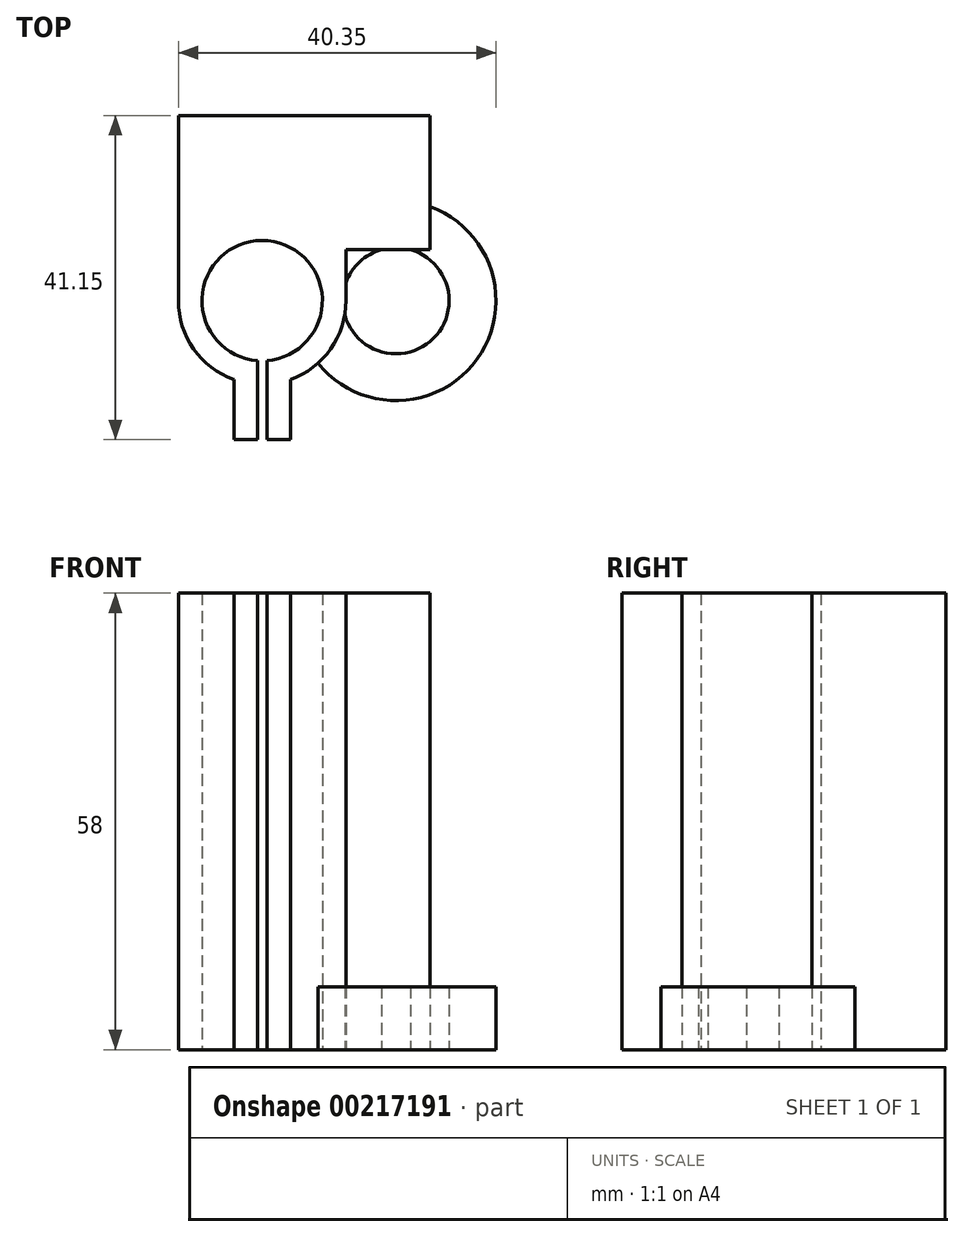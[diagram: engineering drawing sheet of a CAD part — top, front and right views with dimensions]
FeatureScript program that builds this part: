
annotation { "Feature Type Name" : "Feature", "Feature Type Description" : "" }
export const myFeature = defineFeature(function(context is Context, id is Id, definition is map)
    precondition{}
    {
        {
            var Q0;
            Q0=qCreatedBy(makeId("Top.planeOp"),FACE);
            var sketch = newSketch(context, id + "F0", { "sketchPlane" : qUnion([Q0])});
            skCircle(sketch, "E0", {"center": v(0, 0) * mm, "radius": 7.65 * mm});
            skCircle(sketch, "E1.0", {"center": v(0, 0) * mm, "radius": 10.65 * mm});
            skLineSegment(sketch, "E2", {"start": v(-0.6, -7.63) * mm, "end": v(-0.6, -17.65) * mm});
            skLineSegment(sketch, "E3", {"start": v(-0.6, -17.65) * mm, "end": v(-3.6, -17.65) * mm});
            skLineSegment(sketch, "E4", {"start": v(-3.6, -17.65) * mm, "end": v(-3.6, -10.03) * mm});
            skLineSegment(sketch, "E5.MirrorCS", {"start": v(0.6, -7.63) * mm, "end": v(0.6, -17.65) * mm});
            skLineSegment(sketch, "E6.MirrorCS", {"start": v(0.6, -17.65) * mm, "end": v(3.6, -17.65) * mm});
            skLineSegment(sketch, "E7.MirrorCS", {"start": v(3.6, -17.65) * mm, "end": v(3.6, -10.03) * mm});
            skLineSegment(sketch, "E8", {"start": v(21.35, 6.5) * mm, "end": v(21.35, 23.5) * mm});
            skLineSegment(sketch, "E9", {"start": v(-10.65, 0) * mm, "end": v(-10.65, 23.5) * mm});
            skLineSegment(sketch, "E10", {"start": v(-10.65, 23.5) * mm, "end": v(21.35, 23.5) * mm});
            skLineSegment(sketch, "E11", {"start": v(21.35, 6.5) * mm, "end": v(10.65, 6.5) * mm});
            skLineSegment(sketch, "E12", {"start": v(10.65, 0) * mm, "end": v(10.65, 6.5) * mm});
            skSolve(sketch);
        }
        {
            var Q0;
            Q0=makeQuery(id+"F0.imprint","IMPRINT",FACE,{"disambiguationData":[TD([[makeQuery(id+"F0.imprint","IMPRINT",EDGE,{"derivedFrom":sQuery(id+"F0.wireOp",EDGE,"E8")}),1.0]])]});
            var Q1;
            {var subQ2=sQuery(id+"F0.wireOp",EDGE,"E2");var subQ6=sQuery(id+"F0.wireOp",EDGE,"E0");var subQ7=makeQuery(id+"F0.imprint","INTERSECT",VERTEX,{"derivedFrom":[subQ6,subQ2]});Q1=makeQuery(id+"F0.imprint","IMPRINT",FACE,{"disambiguationData":[TD([[makeQuery(id+"F0.imprint","IMPRINT",EDGE,{"disambiguationData":[TD([[subQ7,1.0]])],"derivedFrom":subQ6}),-1.0]])]});}
            var Q2;
            {var subQ4=sQuery(id+"F0.wireOp",EDGE,"E6.MirrorCS");Q2=makeQuery(id+"F0.imprint","IMPRINT",FACE,{"disambiguationData":[TD([[makeQuery(id+"F0.imprint","IMPRINT",EDGE,{"derivedFrom":subQ4}),1.0]])]});}
            var Q3;
            {var subQ4=sQuery(id+"F0.wireOp",EDGE,"E3");Q3=makeQuery(id+"F0.imprint","IMPRINT",FACE,{"disambiguationData":[TD([[makeQuery(id+"F0.imprint","IMPRINT",EDGE,{"derivedFrom":subQ4}),-1.0]])]});}
            extrude(context, id + "F1", {"entities" : qUnion([Q0, Q1, Q2, Q3]), "depth" : 58 * mm});
        }
        {
            var Q0;
            Q0=makeQuery(id+"F1.opExtrude","CAP_FACE",FACE,{"disambiguationData":[OSD([sQuery(id+"F0.wireOp",EDGE,"E0"),sQuery(id+"F0.wireOp",EDGE,"E1.0"),sQuery(id+"F0.wireOp",EDGE,"E2"),sQuery(id+"F0.wireOp",EDGE,"E3"),sQuery(id+"F0.wireOp",EDGE,"E4"),sQuery(id+"F0.wireOp",EDGE,"E5.MirrorCS"),sQuery(id+"F0.wireOp",EDGE,"E6.MirrorCS"),sQuery(id+"F0.wireOp",EDGE,"E7.MirrorCS"),sQuery(id+"F0.wireOp",EDGE,"E8"),sQuery(id+"F0.wireOp",EDGE,"E9"),sQuery(id+"F0.wireOp",EDGE,"E10"),sQuery(id+"F0.wireOp",EDGE,"E11"),sQuery(id+"F0.wireOp",EDGE,"E12")])],"isStart":true});
            var sketch = newSketch(context, id + "F2", { "sketchPlane" : qUnion([Q0])});
            skCircle(sketch, "E13", {"center": v(17, 0) * mm, "radius": 12.7 * mm});
            skCircle(sketch, "E14", {"center": v(17, 0) * mm, "radius": 6.75 * mm});
            skSolve(sketch);
        }
        {
            var Q0;
            {var subQ0=makeQuery(id+"F1.opExtrude","CAP_EDGE",EDGE,{"disambiguationData":[OSD([sQuery(id+"F0.wireOp",EDGE,"E11")])],"isStart":true});var subQ1=makeQuery(id+"F1.opExtrude","CAP_EDGE",EDGE,{"disambiguationData":[OSD([sQuery(id+"F0.wireOp",EDGE,"E8")])],"isStart":true});var subQ2=makeQuery(id+"F2.imprint","INTERSECT",VERTEX,{"derivedFrom":[subQ1,subQ0]});Q0=makeQuery(id+"F2.imprint","IMPRINT",FACE,{"disambiguationData":[TD([[makeQuery(id+"F2.imprint","IMPRINT",EDGE,{"disambiguationData":[TD([[subQ2,-1.0]])],"derivedFrom":subQ1}),1.0]])]});}
            var Q1;
            {var subQ0=sQuery(id+"F2.wireOp",EDGE,"E14");var subQ1=makeQuery(id+"F1.opExtrude","CAP_EDGE",EDGE,{"disambiguationData":[OSD([sQuery(id+"F0.wireOp",EDGE,"E12")])],"isStart":true});var subQ2=makeQuery(id+"F2.imprint","INTERSECT",VERTEX,{"derivedFrom":[subQ1,subQ0]});Q1=makeQuery(id+"F2.imprint","IMPRINT",FACE,{"disambiguationData":[TD([[makeQuery(id+"F2.imprint","IMPRINT",EDGE,{"disambiguationData":[TD([[subQ2,-1.0]])],"derivedFrom":subQ0}),-1.0]])]});}
            extrude(context, id + "F3", {"entities" : qUnion([Q0, Q1]), "operationType" : NewBodyOperationType.ADD, "oppositeDirection" : true, "depth" : 8 * mm});
        }
    });
